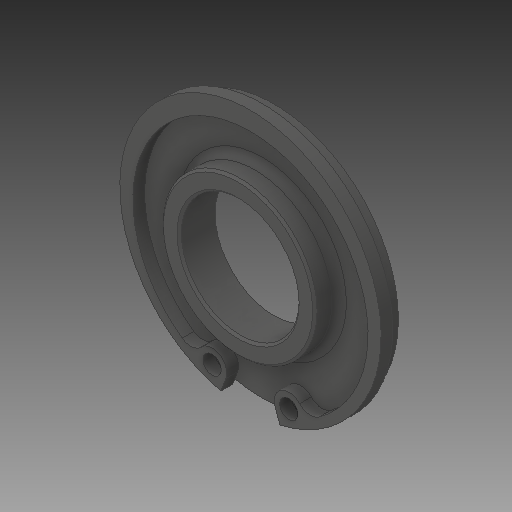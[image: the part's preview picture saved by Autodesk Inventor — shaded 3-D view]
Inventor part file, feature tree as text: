
AUTODESK INVENTOR PART (.ipt)
format: ipt  version: 2017 (Build 210142000, 142)  size: 174,080 bytes
history: native  units: in
note: dims shown in document units (in); Inventor stores cm internally (conversion verified against a paired STEP export)
features: chamfer x1
ambient origin geometry x8: Origin, YZ Plane, XZ Plane, XY Plane, X Axis, Y Axis, Z Axis, Center Point
bodies: Solid1 (feature_tree)
feature tree (1):
  chamfer  "Chamfer1"  [1 undecoded]
note: 1 required parameter value undecoded (feature->parameter linkage not recoverable at this tier; creation-order binding heuristic only, values carry confidence <= 0.55)
